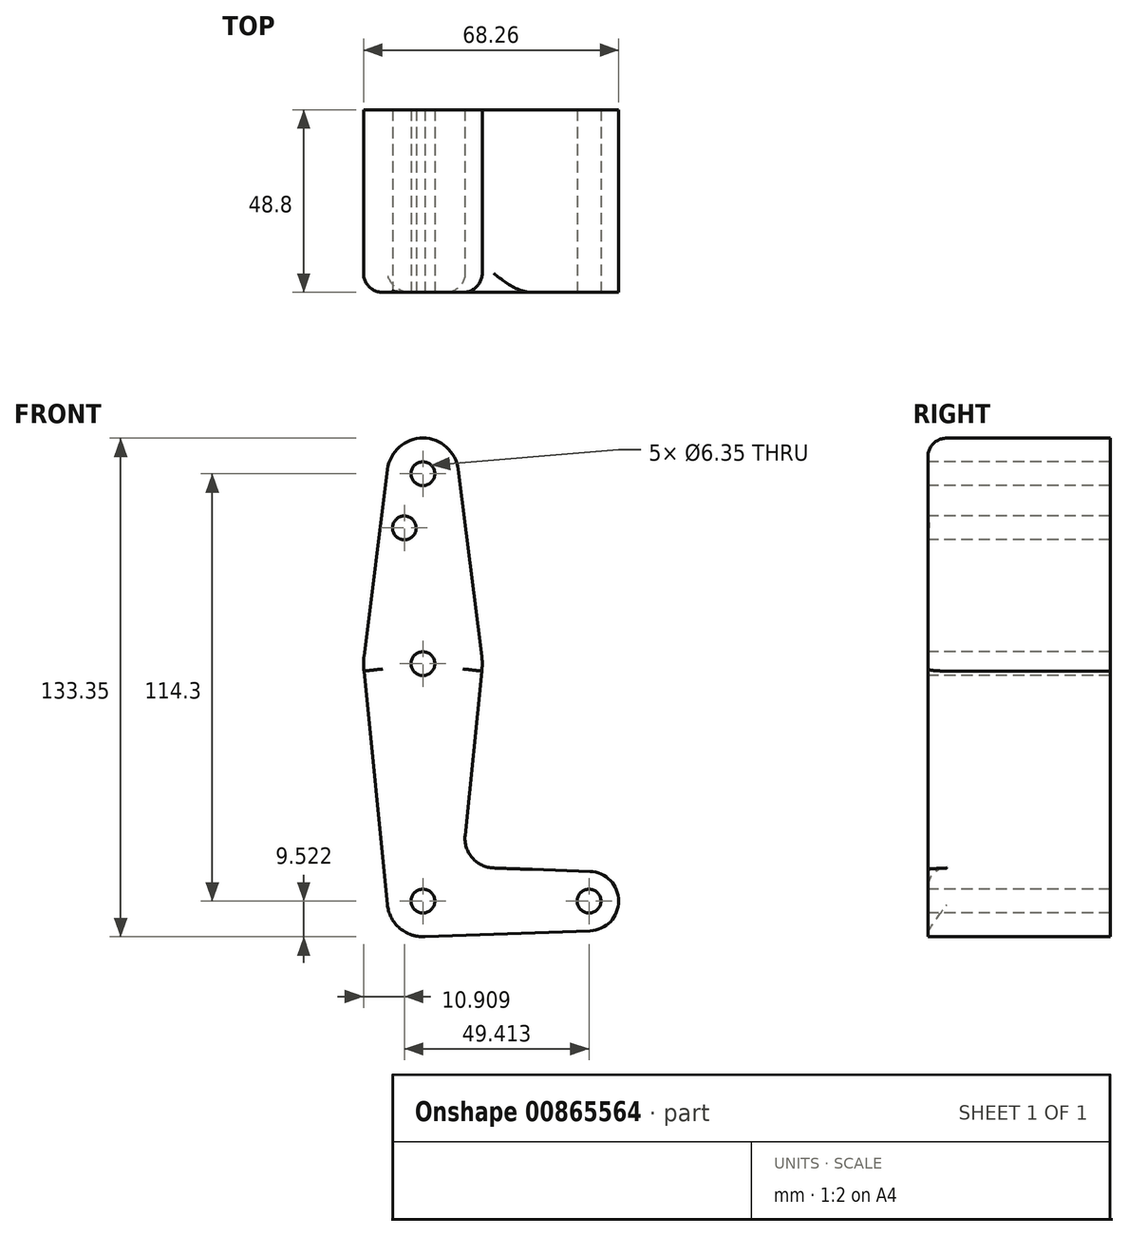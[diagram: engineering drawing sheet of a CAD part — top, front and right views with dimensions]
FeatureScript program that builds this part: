
annotation { "Feature Type Name" : "Feature", "Feature Type Description" : "" }
export const myFeature = defineFeature(function(context is Context, id is Id, definition is map)
    precondition{}
    {
        {
            var Q0;
            Q0=qCreatedBy(makeId("Front.planeOp"),FACE);
            var sketch = newSketch(context, id + "F0", { "sketchPlane" : qUnion([Q0])});
            skLineSegment(sketch, "E0", {"start": v(-32.94, 64.33) * mm, "end": v(-32.94, 13.53) * mm, "construction": true});
            skLineSegment(sketch, "E1", {"start": v(-32.94, 13.53) * mm, "end": v(-32.94, -49.97) * mm, "construction": true});
            skLineSegment(sketch, "E2", {"start": v(-32.94, -49.97) * mm, "end": v(11.51, -49.97) * mm, "construction": true});
            skCircle(sketch, "E3", {"center": v(-32.94, 64.33) * mm, "radius": 9.53 * mm});
            skCircle(sketch, "E4", {"center": v(-32.94, 13.53) * mm, "radius": 15.88 * mm});
            skCircle(sketch, "E5", {"center": v(-32.94, -49.97) * mm, "radius": 9.53 * mm});
            skCircle(sketch, "E6", {"center": v(11.51, -49.97) * mm, "radius": 7.94 * mm});
            skLineSegment(sketch, "E7", {"start": v(-42.39, 65.52) * mm, "end": v(-48.69, 15.52) * mm});
            skLineSegment(sketch, "E8", {"start": v(-48.69, 15.52) * mm, "end": v(-48.69, 11.55) * mm});
            skLineSegment(sketch, "E9", {"start": v(-48.69, 11.55) * mm, "end": v(-42.42, -50.92) * mm});
            skLineSegment(sketch, "E10", {"start": v(-23.49, 65.52) * mm, "end": v(-17.19, 15.52) * mm});
            skLineSegment(sketch, "E11", {"start": v(-17.19, 15.52) * mm, "end": v(-17.19, 11.55) * mm});
            skLineSegment(sketch, "E12", {"start": v(-21.63, -32.37) * mm, "end": v(-17.19, 11.55) * mm});
            skLineSegment(sketch, "E13", {"start": v(-32.38, -59.48) * mm, "end": v(11.8, -57.9) * mm});
            skLineSegment(sketch, "E14", {"start": v(-14, -41.12) * mm, "end": v(11.8, -42.04) * mm});
            skCircle(sketch, "E15", {"center": v(-32.94, 64.33) * mm, "radius": 3.18 * mm});
            skCircle(sketch, "E16", {"center": v(-37.9, 49.85) * mm, "radius": 3.18 * mm});
            skCircle(sketch, "E17", {"center": v(-32.94, 13.53) * mm, "radius": 3.18 * mm});
            skCircle(sketch, "E18", {"center": v(-32.94, -49.97) * mm, "radius": 3.18 * mm});
            skCircle(sketch, "E19", {"center": v(11.51, -49.97) * mm, "radius": 3.18 * mm});
            skArc(sketch, "E20.filletArc", {"start": v(-21.63, -32.37) * mm, "mid": v(-19.71, -38.4) * mm, "end": v(-14, -41.12) * mm});
            skSolve(sketch);
        }
        {
            var Q0;
            Q0 = qSketchRegion(id + "F0", true);
            extrude(context, id + "F1", {"entities" : qUnion([Q0]), "oppositeDirection" : true, "depth" : 48.8 * mm, "offsetDistance" : 25.4 * mm});
        }
        {
            var Q0;
            Q0=makeQuery(id+"F1.opExtrude","CAP_EDGE",EDGE,{"disambiguationData":[OSD([sQuery(id+"F0.wireOp",EDGE,"E7")])],"isStart":true});
            fillet(context, id + "F2", {"entities" : qUnion([Q0]), "radius" : 5.08 * mm, "tangentPropagation" : true, "allowEdgeOverflow" : false});
        }
    });
